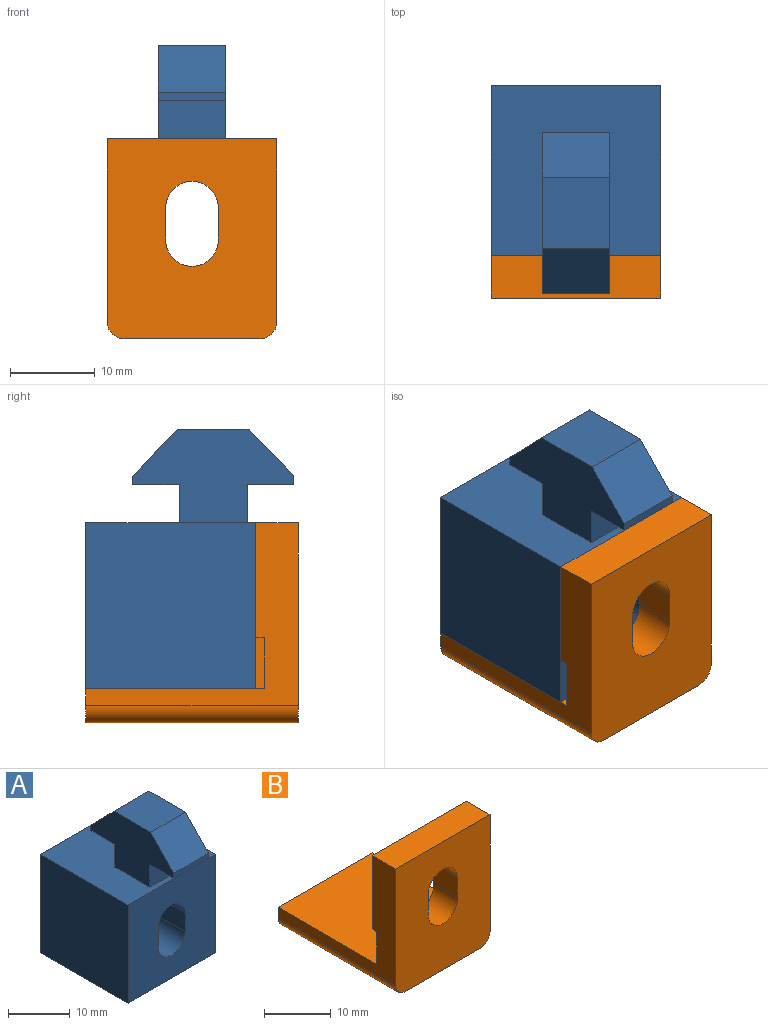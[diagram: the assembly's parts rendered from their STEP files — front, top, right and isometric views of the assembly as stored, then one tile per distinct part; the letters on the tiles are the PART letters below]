
ASSEMBLY  parts=2 mates=1
PART A: 30 faces, bbox 20x24.5x30.5 mm
  f0: plane 9x4mm, normal (0,0,-1), area 36mm2, adj f1,f7,f8,f26
  f1: cylinder r=2mm len=4mm, axis (0,-1,0), area 12.6mm2, adj f0,f2,f8,f26
  f2: plane 10x4mm, normal (-1,0,0), area 40mm2, adj f1,f3,f8,f26
  f3: cylinder r=4mm len=4mm, axis (0,-1,0), area 25.1mm2, adj f2,f4,f8,f26
  f4: plane 5x4mm, normal (0,0,1), area 20mm2, adj f3,f5,f8,f26
  f5: cylinder r=4mm len=4mm, axis (0,-1,0), area 25.1mm2, adj f4,f6,f8,f26
  f6: plane 10x4mm, normal (1,0,0), area 40mm2, adj f5,f7,f8,f26
  f7: cylinder r=2mm len=4mm, axis (0,-1,0), area 12.6mm2, adj f0,f6,f8,f26
  f8: plane 16x13mm, normal (0,1,0), area 145.7mm2, adj f0,f1,f2,f3,f4,f5,f6,f7
  f9: cylinder r=3.1mm len=16mm, axis (0,-1,0), area 155.8mm2, adj f8,f10,f23,f28
  f10: plane 16x3.8mm, normal (-1,0,0), area 60.8mm2, adj f8,f9,f22,f28
  f11: plane 8.42x8mm, normal (0,0,1), area 67.3mm2, adj f12,f19,f20,f21
  f12: plane 8x5.5mm, normal (0,-0.72,0.69), area 61.1mm2, adj f11,f13,f20,f21
  f13: plane 8x1mm, normal (0,-1,0), area 8mm2, adj f12,f14,f20,f21
  f14: plane 8x5.5mm, normal (0,0,-1), area 44mm2, adj f13,f15,f20,f21
  f15: plane 8x4.5mm, normal (0,-1,0), area 36mm2, adj f14,f20,f21,f24
  f16: plane 8x4.5mm, normal (0,1,0), area 36mm2, adj f17,f20,f21,f24
  f17: plane 8x5.5mm, normal (0,0,-1), area 44mm2, adj f16,f18,f20,f21
  f18: plane 8x1mm, normal (0,1,0), area 8mm2, adj f17,f19,f20,f21
  f19: plane 8x5.5mm, normal (0,0.72,0.69), area 61.1mm2, adj f11,f18,f20,f21
  f20: plane 19x11mm, normal (1,0,0), area 130.4mm2, adj f11,f12,f13,f14,f15,f16,f17,f18
  f21: plane 19x11mm, normal (-1,0,0), area 130.4mm2, adj f11,f12,f13,f14,f15,f16,f17,f18
  f22: cylinder r=3.1mm len=16mm, axis (0,-1,0), area 155.8mm2, adj f8,f10,f23,f28
  f23: plane 16x3.8mm, normal (1,0,0), area 60.8mm2, adj f8,f9,f22,f28
  f24: plane 20x20mm, normal (0,0,1), area 336mm2, adj f15,f16,f20,f21,f26,f27,f28,f29
  f25: plane 20x20mm, normal (0,0,-1), area 400mm2, adj f26,f27,f28,f29
  f26: plane 20x19.5mm, normal (0,1,0), area 190.6mm2, adj f0,f1,f2,f3,f4,f5,f6,f7
  f27: plane 20x19.5mm, normal (1,0,0), area 390mm2, adj f24,f25,f26,f28
  f28: plane 20x19.5mm, normal (0,-1,0), area 336.2mm2, adj f9,f10,f22,f23,f24,f25,f27,f29
  f29: plane 20x19.5mm, normal (-1,0,0), area 390mm2, adj f24,f25,f26,f28
PART B: 20 faces, bbox 20x25x23.5 mm
  f0: plane 5x1mm, normal (0,0,-1), area 5mm2, adj f1,f2,f3,f12
  f1: plane 6x5mm, normal (0,1,0), area 30mm2, adj f0,f2,f12,f17
  f2: plane 6x1mm, normal (1,0,0), area 6mm2, adj f0,f1,f3,f17
  f3: plane 20x19.5mm, normal (0,1,0), area 276.2mm2, adj f0,f2,f4,f6,f7,f12,f13,f14
  f4: plane 5x1mm, normal (0,0,-1), area 5mm2, adj f3,f5,f6,f7
  f5: plane 6x5mm, normal (0,1,0), area 30mm2, adj f4,f6,f7,f17
  f6: plane 6x1mm, normal (-1,0,0), area 6mm2, adj f3,f4,f5,f17
  f7: plane 25x21.5mm, normal (-1,0,0), area 141.5mm2, adj f3,f4,f5,f8,f10,f17,f18,f19
  f8: cylinder r=2mm len=25mm, axis (0,1,0), area 78.5mm2, adj f7,f9,f10,f19
  f9: plane 25x16mm, normal (0,0,-1), area 400mm2, adj f8,f10,f11,f19
  f10: plane 20x4mm, normal (0,1,0), area 78.3mm2, adj f7,f8,f9,f11,f12,f17
  f11: cylinder r=2mm len=25mm, axis (0,1,0), area 78.5mm2, adj f9,f10,f12,f19
  f12: plane 25x21.5mm, normal (1,0,0), area 141.5mm2, adj f0,f1,f3,f10,f11,f17,f18,f19
  f13: plane 5x3.8mm, normal (-1,0,0), area 19mm2, adj f3,f14,f16,f19
  f14: cylinder r=3.1mm len=6.2mm, axis (0,1,0), area 48.7mm2, adj f3,f13,f15,f19
  f15: plane 5x3.8mm, normal (1,0,0), area 19mm2, adj f3,f14,f16,f19
  f16: cylinder r=3.1mm len=6.2mm, axis (0,1,0), area 48.7mm2, adj f3,f13,f15,f19
  f17: plane 21x20mm, normal (0,0,1), area 410mm2, adj f1,f2,f3,f5,f6,f7,f10,f12
  f18: plane 20x5mm, normal (0,0,1), area 100mm2, adj f3,f7,f12,f19
  f19: plane 23.5x20mm, normal (0,-1,0), area 414.5mm2, adj f7,f8,f9,f11,f12,f13,f14,f15
PLACE A at identity fixed
PLACE B at identity
MATE fastened A.f28 <-> B.f3  axis (0,-1,0) through (10,-15,0)mm
